# Revit family: PROOX Soap- desinfection dispenser EN
name_source: partatom
category: Furniture
revit_build: Autodesk Revit 2014 (Build: 20130308_1515(x64)
units: mm (PartAtom-declared; Revit-internal decimal feet)

## types (2) — shared parameters
BIM objects producer = www.BIMtelligent.eu
Manufacturer = PROOX Ltd.
Product data sheet = http://www.proox.com
URL = http://www.proox.com

## per-type parameters (varying)
| type | Cost | Description | EAN-No. | Material | Model | Specification |
| ONE pure | 215 $ | soap- desinfection dispenser PROOX ONE pure made from stainless steel | 9120050350045 | Stainless steel, brushed | PU-140 | Soap- desinfection dispenser made out of stainless steel. Surface with fine brushed structure. Cover 1.5 mm thickness. Intended for wall mounting. Perforated fill level indicator with 4mm drillings. Soap dispenser lever made out of stainless steel. High quality pump. Filling bin with lid. 1.2 litres capacity. The unit can be dismounted for cleaning purpose. Lock not visible. Includes stainless steel screws and anchors. |
| ONE dark passion | 245 $ | soap-desinfection dispenser PROOX ONE dark passion made from aluminum black anodized | 9120050350182 | Aluminum, black anodised | DP-140 | Soap- desinfection dispenser made out from glass pearl blasted and black anodised aluminum. Cover 3 mm thickness. Intended for wall mounting. Perforated fill level indicator with 4mm drillings. Soap dispenser lever made out of stainless steel. High quality pump. Filling bin with lid. 1.2 litres capacity. The unit can be dismounted for cleaning purpose. Lock not visible. Includes stainless steel screws and anchors. |

note: column(s) folded — value = type name in every type: Type Comments

## geometry (parser evidence)
native form markers: Sweep x1
no freeform markers — native parametric forms only
